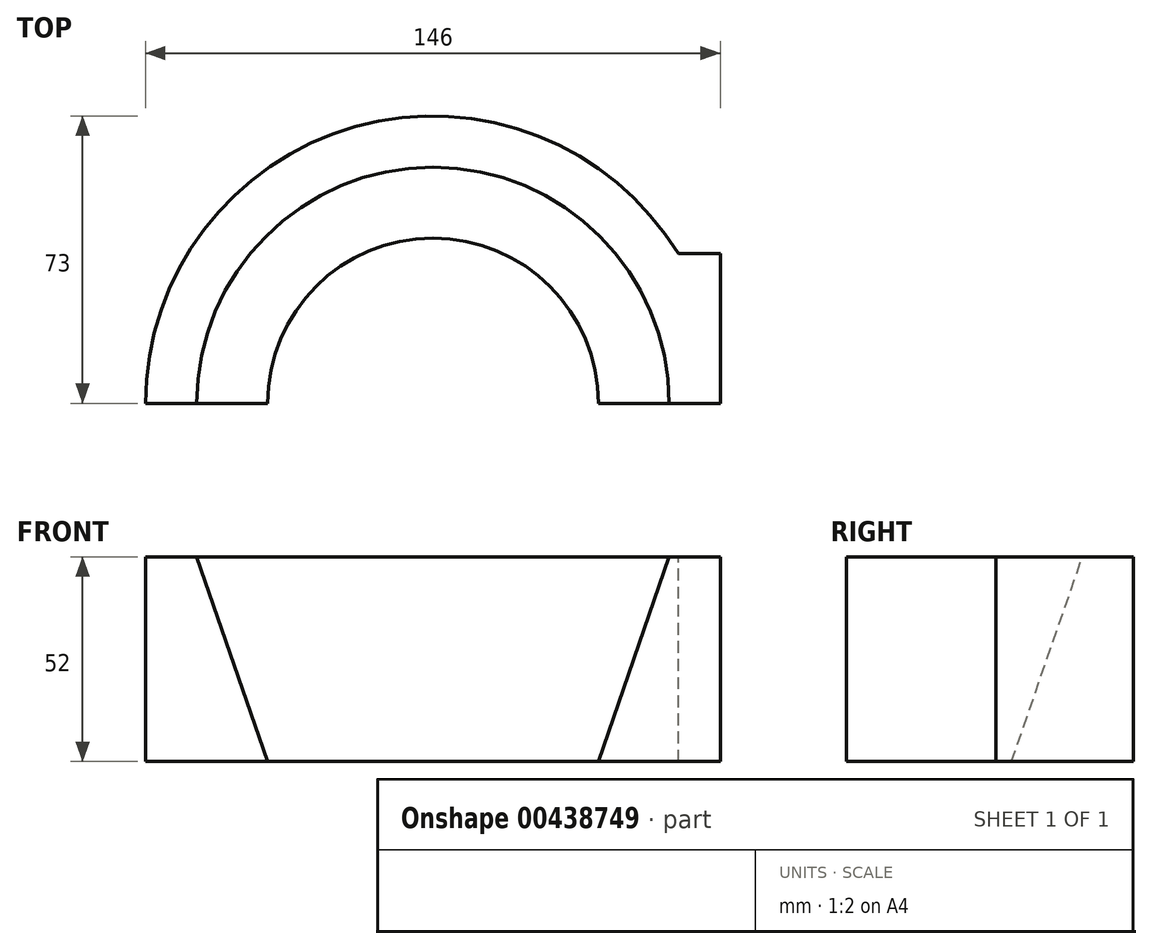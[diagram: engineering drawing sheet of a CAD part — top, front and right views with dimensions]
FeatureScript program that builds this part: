
annotation { "Feature Type Name" : "Feature", "Feature Type Description" : "" }
export const myFeature = defineFeature(function(context is Context, id is Id, definition is map)
    precondition{}
    {
        {
            var Q0;
            Q0=qCreatedBy(makeId("Front.planeOp"),FACE);
            var sketch = newSketch(context, id + "F0", { "sketchPlane" : qUnion([Q0])});
            skLineSegment(sketch, "E0", {"start": v(0, 45.4) * mm, "end": v(0, -49.2) * mm, "construction": true});
            skLineSegment(sketch, "E1", {"start": v(-73, 0) * mm, "end": v(-73, 52) * mm});
            skLineSegment(sketch, "E2", {"start": v(-73, 52) * mm, "end": v(-60, 52) * mm});
            skLineSegment(sketch, "E3", {"start": v(-60, 52) * mm, "end": v(-42, 0) * mm});
            skLineSegment(sketch, "E4", {"start": v(-73, 0) * mm, "end": v(-42, 0) * mm});
            skSolve(sketch);
        }
        {
            var Q0;
            Q0=makeQuery(id+"F0.imprint","IMPRINT",FACE,{"disambiguationData":[TD([[makeQuery(id+"F0.imprint","IMPRINT",EDGE,{"derivedFrom":sQuery(id+"F0.wireOp",EDGE,"E1")}),-1.0]])]});
            var Q1;
            Q1=sQuery(id+"F0.wireOp",EDGE,"E0");
            revolve(context, id + "F1", {"entities" : qUnion([Q0]), "axis" : qUnion([Q1]), "revolveType" : RevolveType.ONE_DIRECTION, "angle" : 180 * degree});
        }
        {
            var Q0;
            Q0=makeQuery(id+"F1.opRevolve","CAP_FACE",FACE,{"disambiguationData":[OSD([sQuery(id+"F0.wireOp",EDGE,"E1"),sQuery(id+"F0.wireOp",EDGE,"E2"),sQuery(id+"F0.wireOp",EDGE,"E3"),sQuery(id+"F0.wireOp",EDGE,"E4")])],"isStart":false});
            var sketch = newSketch(context, id + "F2", { "sketchPlane" : qUnion([Q0])});
            skLineSegment(sketch, "E5", {"start": v(60, 52) * mm, "end": v(156, 52) * mm});
            skLineSegment(sketch, "E6", {"start": v(156, 52) * mm, "end": v(156, 0) * mm, "construction": true});
            skLineSegment(sketch, "E7", {"start": v(156, 0) * mm, "end": v(42, 0) * mm});
            skLineSegment(sketch, "E8.0", {"start": v(60, 52) * mm, "end": v(42, 0) * mm});
            skArc(sketch, "E9", {"start": v(156, 52) * mm, "mid": v(182, 26) * mm, "end": v(156, 0) * mm});
            skLineSegment(sketch, "E10", {"start": v(0, 0) * mm, "end": v(0, 77.67) * mm});
            skCircle(sketch, "E11", {"center": v(156, 26) * mm, "radius": 11 * mm});
            skCircle(sketch, "E12", {"center": v(108, 26) * mm, "radius": 11 * mm});
            skSolve(sketch);
        }
        {
            var Q0;
            {var subQ2=sQuery(id+"F2.wireOp",EDGE,"E8.0");Q0=makeQuery(id+"F2.imprint","IMPRINT",FACE,{"disambiguationData":[TD([[makeQuery(id+"F2.imprint","IMPRINT",EDGE,{"derivedFrom":subQ2}),1.0]])]});}
            var Q1;
            {var subQ0=sQuery(id+"F2.wireOp",EDGE,"E9");Q1=makeQuery(id+"F2.imprint","IMPRINT",FACE,{"disambiguationData":[TD([[makeQuery(id+"F2.imprint","IMPRINT",EDGE,{"derivedFrom":subQ0}),-1.0]])]});}
            extrude(context, id + "F3", {"entities" : qUnion([Q0, Q1]), "operationType" : NewBodyOperationType.ADD, "oppositeDirection" : true, "depth" : 38 * mm});
        }
    });
